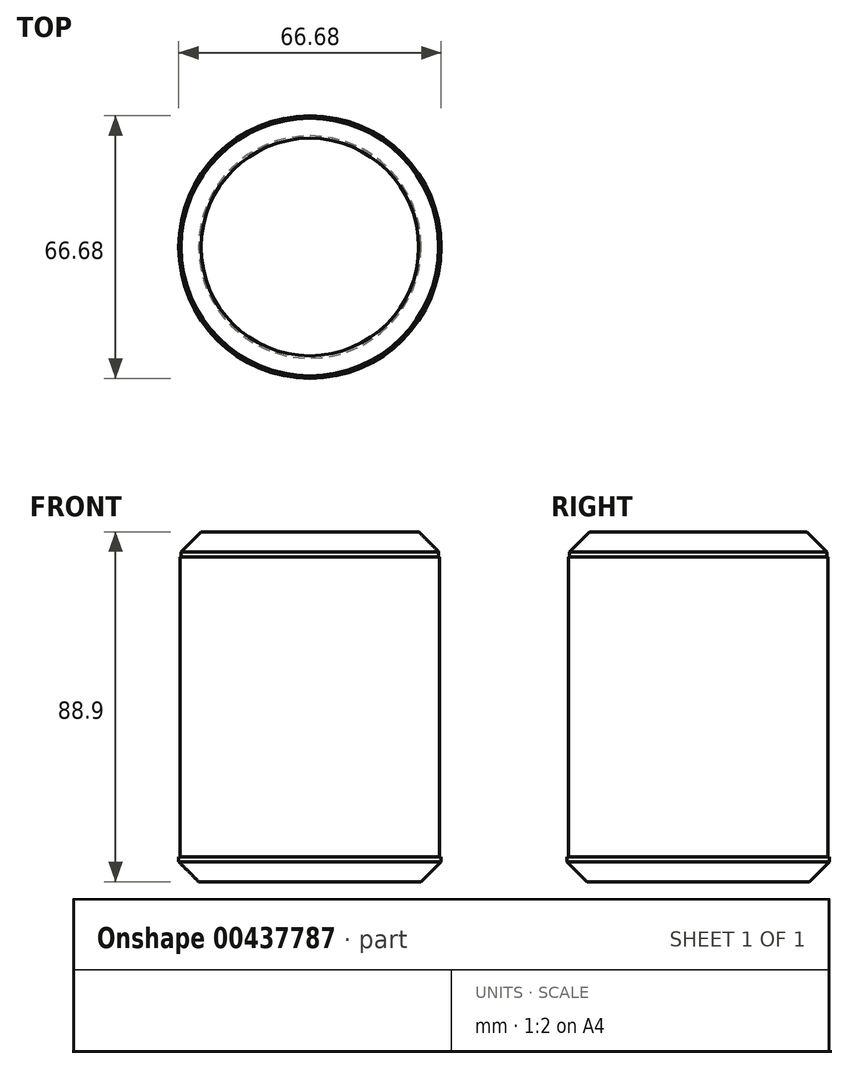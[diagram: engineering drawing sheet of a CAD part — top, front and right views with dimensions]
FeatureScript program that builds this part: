
annotation { "Feature Type Name" : "Feature", "Feature Type Description" : "" }
export const myFeature = defineFeature(function(context is Context, id is Id, definition is map)
    precondition{}
    {
        {
            var Q0;
            Q0=qCreatedBy(makeId("Top.planeOp"),FACE);
            var sketch = newSketch(context, id + "F0", { "sketchPlane" : qUnion([Q0])});
            skCircle(sketch, "E0", {"center": v(0, 0) * mm, "radius": 32.72 * mm});
            skSolve(sketch);
        }
        {
            var Q0;
            Q0 = qSketchRegion(id + "F0", true);
            extrude(context, id + "F1", {"entities" : qUnion([Q0]), "depth" : 6.35 * mm});
        }
        {
            var Q0;
            Q0=makeQuery(id+"F1.opExtrude","CAP_FACE",FACE,{"disambiguationData":[OSD([sQuery(id+"F0.wireOp",EDGE,"E0")])],"isStart":false});
            chamfer(context, id + "F2", {"entities" : qUnion([Q0]), "width" : 5.08 * mm, "tangentPropagation" : true});
        }
        {
            var Q0;
            Q0=makeQuery(id+"F1.opExtrude","CAP_FACE",FACE,{"disambiguationData":[OSD([sQuery(id+"F0.wireOp",EDGE,"E0")])],"isStart":true});
            var sketch = newSketch(context, id + "F3", { "sketchPlane" : qUnion([Q0])});
            skCircle(sketch, "E1", {"center": v(0, 0) * mm, "radius": 32.94 * mm});
            skSolve(sketch);
        }
        {
            var Q0;
            Q0 = qSketchRegion(id + "F3", true);
            extrude(context, id + "F4", {"entities" : qUnion([Q0]), "operationType" : NewBodyOperationType.ADD, "depth" : 76.2 * mm});
        }
        {
            var Q0;
            Q0=makeQuery(id+"F4.opExtrude","CAP_FACE",FACE,{"disambiguationData":[OSD([sQuery(id+"F3.wireOp",EDGE,"E1")])],"isStart":false});
            var sketch = newSketch(context, id + "F5", { "sketchPlane" : qUnion([Q0])});
            skCircle(sketch, "E2", {"center": v(0, 0) * mm, "radius": 33.34 * mm});
            skSolve(sketch);
        }
        {
            var Q0;
            Q0 = qSketchRegion(id + "F5", true);
            extrude(context, id + "F6", {"entities" : qUnion([Q0]), "operationType" : NewBodyOperationType.ADD, "depth" : 6.35 * mm});
        }
        {
            var Q0;
            Q0=makeQuery(id+"F6.opExtrude","CAP_FACE",FACE,{"disambiguationData":[OSD([sQuery(id+"F5.wireOp",EDGE,"E2")])],"isStart":false});
            chamfer(context, id + "F7", {"entities" : qUnion([Q0]), "width" : 5.08 * mm, "tangentPropagation" : true});
        }
    });
